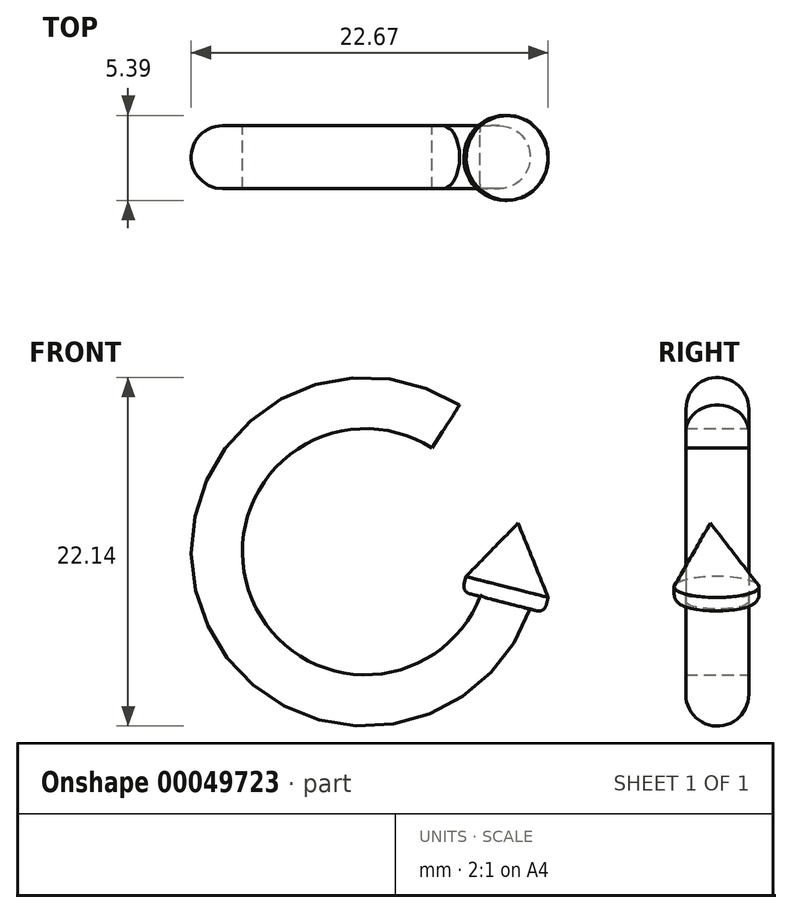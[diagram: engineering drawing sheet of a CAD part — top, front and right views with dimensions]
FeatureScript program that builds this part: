
annotation { "Feature Type Name" : "Feature", "Feature Type Description" : "" }
export const myFeature = defineFeature(function(context is Context, id is Id, definition is map)
    precondition{}
    {
        {
            var Q0;
            Q0=qCreatedBy(makeId("Front.planeOp"),FACE);
            var sketch = newSketch(context, id + "F0", { "sketchPlane" : qUnion([Q0])});
            skArc(sketch, "E0", {"start": v(4.77, 0) * mm, "mid": v(-11.5, -13.4) * mm, "end": v(9.53, -12) * mm});
            skCircle(sketch, "E1", {"center": v(-1.21, -9.32) * mm, "radius": 7.82 * mm});
            skLineSegment(sketch, "E2", {"start": v(4.77, 0) * mm, "end": v(-1.21, -9.32) * mm});
            skLineSegment(sketch, "E3", {"start": v(-0.55, -9.44) * mm, "end": v(9.53, -12) * mm});
            skSolve(sketch);
        }
        {
            var Q0;
            {var subQ3=sQuery(id+"F0.wireOp",EDGE,"E0");Q0=makeQuery(id+"F0.imprint","IMPRINT",FACE,{"disambiguationData":[TD([[makeQuery(id+"F0.imprint","IMPRINT",EDGE,{"derivedFrom":subQ3}),1.0]])]});}
            extrude(context, id + "F1", {"entities" : qUnion([Q0]), "depth" : 4 * mm});
        }
        {
            var Q0;
            Q0=makeQuery(id+"F1.opExtrude","CAP_EDGE",EDGE,{"disambiguationData":[OSD([sQuery(id+"F0.wireOp",EDGE,"E0")])],"isStart":false});
            var Q1;
            Q1=makeQuery(id+"F1.opExtrude","CAP_EDGE",EDGE,{"disambiguationData":[OSD([sQuery(id+"F0.wireOp",EDGE,"E0")])],"isStart":true});
            fillet(context, id + "F2", {"entities" : qUnion([Q0, Q1]), "radius" : 2 * mm, "tangentPropagation" : true, "allowEdgeOverflow" : false});
        }
        {
            var Q0;
            Q0=makeQuery(id+"F1.opExtrude","SWEPT_FACE",FACE,{"disambiguationData":[OSD([sQuery(id+"F0.wireOp",EDGE,"E3")])]});
            var sketch = newSketch(context, id + "F3", { "sketchPlane" : qUnion([Q0])});
            skCircle(sketch, "E4", {"center": v(10.39, -2.04) * mm, "radius": 2.7 * mm});
            skSolve(sketch);
        }
        {
            var Q0;
            Q0=qCreatedBy(makeId("Top.planeOp"),FACE);
            cPlane(context, id + "F4", {"entities" : qUnion([Q0]), "cplaneType" : CPlaneType.OFFSET, "offset" : 5 * mm, "oppositeDirection" : true, "width" : 150 * mm, "height" : 150 * mm});
        }
        {
            var Q0;
            Q0=makeQuery(id+"F3.imprint","IMPRINT",FACE,{"disambiguationData":[TD([[makeQuery(id+"F3.imprint","IMPRINT",EDGE,{"derivedFrom":sQuery(id+"F3.wireOp",EDGE,"E4")}),1.0]])]});
            var Q1;
            {var subQ0=sQuery(id+"F0.wireOp",EDGE,"E3");Q1=makeQuery(id+"F3.imprint","IMPRINT",FACE,{"disambiguationData":[TD([[makeQuery(id+"F3.imprint","IMPRINT",EDGE,{"derivedFrom":makeQuery(id+"F1.opExtrude","CAP_EDGE",EDGE,{"disambiguationData":[OSD([subQ0])],"isStart":true})}),-1.0]])]});}
            extrude(context, id + "F5", {"entities" : qUnion([Q0, Q1]), "operationType" : NewBodyOperationType.ADD, "oppositeDirection" : true, "depth" : 1 * mm});
        }
        {
            var Q0;
            Q0=makeQuery(id+"F5.opExtrude","CAP_EDGE",EDGE,{"disambiguationData":[OSD([sQuery(id+"F3.wireOp",EDGE,"E4")])],"isStart":false});
            fillet(context, id + "F6", {"entities" : qUnion([Q0]), "radius" : 0.5 * mm, "tangentPropagation" : true, "allowEdgeOverflow" : false});
        }
        {
            var Q0;
            Q0=qCreatedBy(id+"F4.planeOp",FACE);
            cPlane(context, id + "F7", {"entities" : qUnion([Q0]), "cplaneType" : CPlaneType.OFFSET, "offset" : 2.5 * mm, "oppositeDirection" : true, "width" : 150 * mm, "height" : 150 * mm});
        }
        {
            var Q0;
            Q0=qCreatedBy(id+"F7.planeOp",FACE);
            var sketch = newSketch(context, id + "F8", { "sketchPlane" : qUnion([Q0])});
            skCircle(sketch, "E5", {"center": v(8.48, -2.44) * mm, "radius": 3.25 * mm});
            skSolve(sketch);
        }
        {
            var Q0;
            Q0=makeQuery(id+"F5.boolean.opBoolean","MERGE",FACE,{"derivedFrom":[makeQuery(id+"F1.opExtrude","SWEPT_FACE",FACE,{"disambiguationData":[OSD([sQuery(id+"F0.wireOp",EDGE,"E3")])]}),makeQuery(id+"F5.opExtrude","CAP_FACE",FACE,{"disambiguationData":[OSD([sQuery(id+"F3.wireOp",EDGE,"E4")])],"isStart":true})]});
            var Q1;
            Q1=sQuery(id+"F8.wireOp",VERTEX,"E5.center");
            loft(context, id + "F9", {"sheetProfilesArray" : [{ "sheetProfileEntities" : qUnion([Q0]) }, { "sheetProfileEntities" : qUnion([Q1]) }]});
        }
    });
